# Revit family: PP-6_GENERADO
name_source: partatom
category: Equipos mecánicos
revit_build: Autodesk Revit 2014 (Build: 20130308_1515(x64)
units: mm (PartAtom-declared; Revit-internal decimal feet)

## types (6) — shared parameters
Depth = 700 mm  [stored 2.29659 ft]
Fabricante = SAMMIC S.L.
Foodservice Equipment Identifier = Sí
Height = 433 mm  [stored 1.4206 ft]
Revision Code = 1
Specification by Manufacturer = PPC: Equipped with attachment drive to power accessories.
URL = https://www.sammic.com
URL Cutsheet = http://www.sammic.com
Weight in Pounds = 68.3
Width = 395 mm  [stored 1.29593 ft]

## per-type parameters (varying)
| type | Comentarios de tipo | Cycle | Electric Connection Type | FL Amps | Modelo | Volts |
| Potato peeler PP-6+ 230-400/50/3 ·370W | Output: 6 Kg. per cycle. Aluminium made potato peeler.

ELECTRICAL DATA:

230V/50Hz/3~ (1.9A) | 50 Hz |  | 1 A | 1000410 | 400 V |
| Potato peeler PP-6+ 230/50/1 ·400W | Output: 6 Kg. per cycle. Aluminium made potato peeler. | 50 Hz |  | 2 A | 1000411 | 230 V |
| Potato peeler PP-6+ 220-380/60/3 | Output: 6 Kg. per cycle. Aluminium made potato peeler.

ELECTRICAL DATA:

380V/60Hz/3~ (1.4A) | 60 Hz |  | 2 A | 1000412 | 220 V |
| Potato peeler PP-6+ 220/60/1 | Output: 6 Kg. per cycle. Aluminium made potato peeler. | 60 Hz |  | 3 A | 1000413 | 220 V |
| Potato peeler PP-6+ 120/60/1 | Output: 6 Kg. per cycle. Aluminium made potato peeler. | 60 Hz | USA | 6 A | 1000414 | 120 V |
| Potato peeler PP-6+ 440/60/3 | Output: 6 Kg. per cycle. Aluminium made potato peeler. | 60 Hz |  | 1 A | 1000417 | 440 V |

note: column(s) folded — value = type name in every type: Descripción

note: [stored X ft] marks values corroborated as IEEE doubles in the binary element streams (Revit-internal decimal feet)
